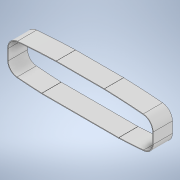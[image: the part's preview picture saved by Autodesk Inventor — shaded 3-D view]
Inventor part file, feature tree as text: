
AUTODESK INVENTOR PART (.ipt)
format: ipt  version: 2021 (Build 250183000, 183)  size: 193,536 bytes
history: native  units: mm
features: other x2, extrude x1, sketch x1
ambient origin geometry x8: Origin, YZ Plane, XZ Plane, XY Plane, X Axis, Y Axis, Z Axis, Center Point
bodies: Body1 (feature_tree)
feature tree (4):
  other  "Blocks"
  extrude  "Extrusion2"  Depth=600.0mm
  sketch  "Sketch2"  dims[d0=600.0mm d1=200.0mm d2=143.0mm d3=200.0mm d4=20.0mm d5=42.0mm d6=40.0mm d7=40.0mm d8=42.0mm d9=10.0mm d10=140.0mm d11=10.0mm d12=140.0mm d13=120.0mm d14=120.0mm d20=200.0mm d21=320.0mm d22=13.0mm d23=13.0mm d44=143.0mm d47=600.0mm d50=600.0mm d51=120.0mm d52=120.0mm d53=140.0mm d54=140.0mm d55=200.0mm d56=200.0mm d57=200.0mm d58=320.0mm d59=143.0mm d60=10.0mm d61=10.0mm d62=13.0mm d63=13.0mm d64=42.0mm d65=40.0mm d66=40.0mm d67=42.0mm d68=20.0mm d69=3.0mm d70=80.0mm d71=0.0mm]
  other  "Block1"
